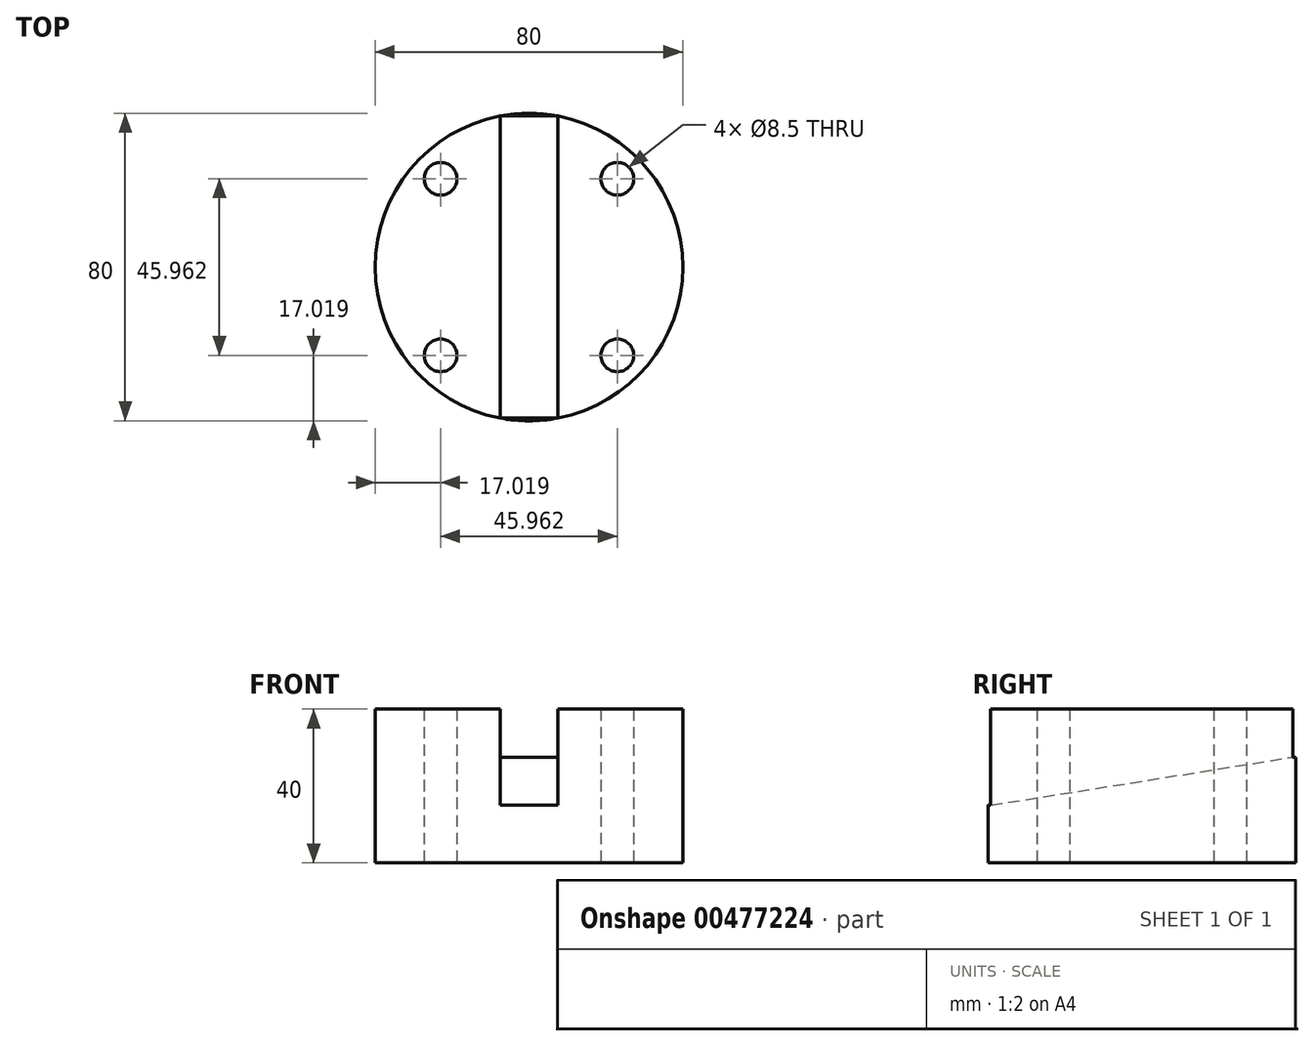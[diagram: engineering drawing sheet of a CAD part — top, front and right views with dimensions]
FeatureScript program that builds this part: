
annotation { "Feature Type Name" : "Feature", "Feature Type Description" : "" }
export const myFeature = defineFeature(function(context is Context, id is Id, definition is map)
    precondition{}
    {
        {
            var Q0;
            Q0=qCreatedBy(makeId("Top.planeOp"),FACE);
            var sketch = newSketch(context, id + "F0", { "sketchPlane" : qUnion([Q0])});
            skCircle(sketch, "E0", {"center": v(0, 0) * mm, "radius": 40 * mm});
            skCircle(sketch, "E1", {"center": v(0, 0) * mm, "radius": 32.5 * mm, "construction": true});
            skLineSegment(sketch, "E2", {"start": v(-45.9, 45.9) * mm, "end": v(37.06, -37.06) * mm, "construction": true});
            skLineSegment(sketch, "E3", {"start": v(-46.49, -46.49) * mm, "end": v(56.1, 56.1) * mm, "construction": true});
            skCircle(sketch, "E4", {"center": v(-22.98, 22.98) * mm, "radius": 4.25 * mm});
            skCircle(sketch, "E5", {"center": v(22.98, 22.98) * mm, "radius": 4.25 * mm});
            skCircle(sketch, "E6", {"center": v(22.98, -22.98) * mm, "radius": 4.25 * mm});
            skCircle(sketch, "E7", {"center": v(-22.98, -22.98) * mm, "radius": 4.25 * mm});
            skSolve(sketch);
        }
        {
            var Q0;
            Q0=makeQuery(id+"F0.imprint","IMPRINT",FACE,{"disambiguationData":[TD([[makeQuery(id+"F0.imprint","IMPRINT",EDGE,{"derivedFrom":sQuery(id+"F0.wireOp",EDGE,"E0")}),1.0]])]});
            extrude(context, id + "F1", {"entities" : qUnion([Q0]), "depth" : 40 * mm});
        }
        {
            var Q0;
            Q0=makeQuery(id+"F1.opExtrude","CAP_FACE",FACE,{"disambiguationData":[OSD([sQuery(id+"F0.wireOp",EDGE,"E0"),sQuery(id+"F0.wireOp",EDGE,"E4"),sQuery(id+"F0.wireOp",EDGE,"E5"),sQuery(id+"F0.wireOp",EDGE,"E6"),sQuery(id+"F0.wireOp",EDGE,"E7")])],"isStart":false});
            var sketch = newSketch(context, id + "F2", { "sketchPlane" : qUnion([Q0])});
            skLineSegment(sketch, "E8.bottom", {"start": v(-7.5, 40) * mm, "end": v(7.5, 40) * mm});
            skLineSegment(sketch, "E8.top", {"start": v(-7.5, -40) * mm, "end": v(7.5, -40) * mm});
            skLineSegment(sketch, "E8.left", {"start": v(-7.5, 40) * mm, "end": v(-7.5, -40) * mm});
            skLineSegment(sketch, "E8.right", {"start": v(7.5, 40) * mm, "end": v(7.5, -40) * mm});
            skSolve(sketch);
        }
        {
            var Q0;
            Q0 = qSketchRegion(id + "F2", true);
            extrude(context, id + "F3", {"entities" : qUnion([Q0]), "operationType" : NewBodyOperationType.REMOVE, "oppositeDirection" : true, "depth" : 25 * mm});
        }
        {
            var Q0;
            Q0=makeQuery(id+"F3.boolean.opBoolean","COPY",FACE,{"derivedFrom":makeQuery(id+"F3.opExtrude","SWEPT_FACE",FACE,{"disambiguationData":[OSD([sQuery(id+"F2.wireOp",EDGE,"E8.left")])]})});
            var sketch = newSketch(context, id + "F4", { "sketchPlane" : qUnion([Q0])});
            skLineSegment(sketch, "E9", {"start": v(-39.3, 15) * mm, "end": v(39.3, 27.5) * mm});
            skLineSegment(sketch, "E10", {"start": v(39.3, 27.5) * mm, "end": v(39.3, 15) * mm});
            skLineSegment(sketch, "E11", {"start": v(39.3, 15) * mm, "end": v(-39.3, 15) * mm});
            skSolve(sketch);
        }
        {
            var Q0;
            Q0 = qSketchRegion(id + "F4", true);
            extrude(context, id + "F5", {"entities" : qUnion([Q0]), "operationType" : NewBodyOperationType.ADD, "depth" : 15 * mm});
        }
        {
            var Q0;
            Q0=makeQuery(id+"F5.boolean.opBoolean","SPLIT",FACE,{"disambiguationData":[TD([makeQuery(id+"F5.opExtrude","SWEPT_FACE",FACE,{"disambiguationData":[OSD([sQuery(id+"F4.wireOp",EDGE,"E10")])]})])],"derivedFrom":makeQuery(id+"F3.boolean.opBoolean","COPY",FACE,{"derivedFrom":makeQuery(id+"F3.opExtrude","CAP_FACE",FACE,{"disambiguationData":[OSD([sQuery(id+"F2.wireOp",EDGE,"E8.bottom"),sQuery(id+"F2.wireOp",EDGE,"E8.top"),sQuery(id+"F2.wireOp",EDGE,"E8.left"),sQuery(id+"F2.wireOp",EDGE,"E8.right")])],"isStart":false})})});
            var sketch = newSketch(context, id + "F6", { "sketchPlane" : qUnion([Q0])});
            skLineSegment(sketch, "E12.0", {"start": v(-7.5, 39.3) * mm, "end": v(7.5, 39.3) * mm});
            skArc(sketch, "E12.1", {"start": v(7.5, 39.3) * mm, "mid": v(0, 40) * mm, "end": v(-7.5, 39.3) * mm});
            skSolve(sketch);
        }
        {
            var Q0;
            Q0 = qSketchRegion(id + "F6", true);
            extrude(context, id + "F7", {"entities" : qUnion([Q0]), "operationType" : NewBodyOperationType.ADD, "depth" : 12.5 * mm});
        }
    });
